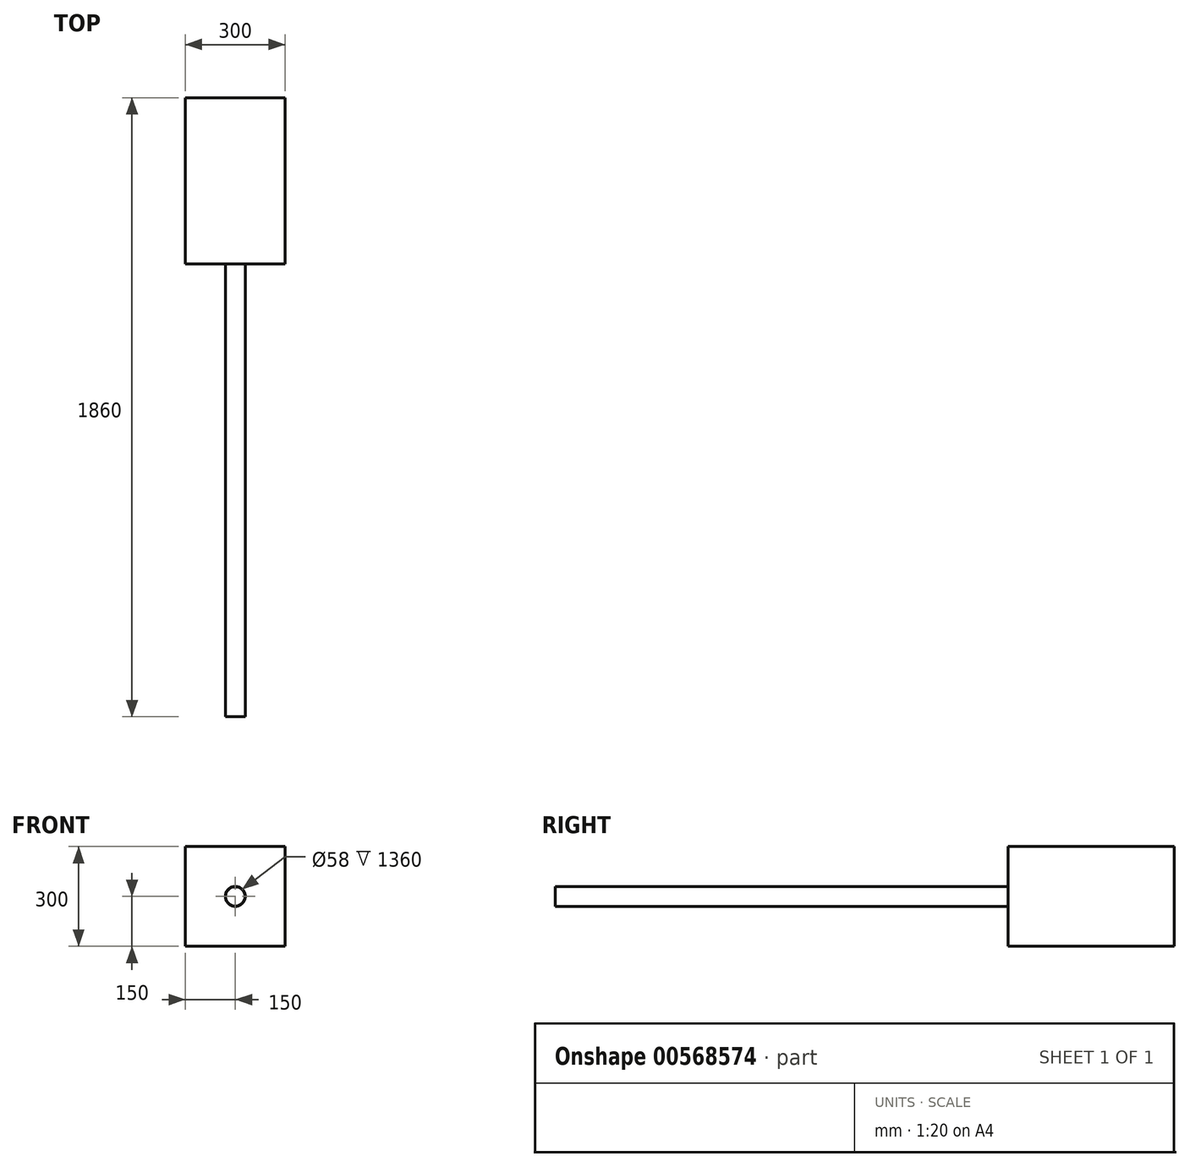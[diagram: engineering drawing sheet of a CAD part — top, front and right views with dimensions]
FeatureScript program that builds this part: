
annotation { "Feature Type Name" : "Feature", "Feature Type Description" : "" }
export const myFeature = defineFeature(function(context is Context, id is Id, definition is map)
    precondition{}
    {
        {
            var Q0;
            Q0=qCreatedBy(makeId("Front.planeOp"),FACE);
            var sketch = newSketch(context, id + "F0", { "sketchPlane" : qUnion([Q0])});
            skCircle(sketch, "E0", {"center": v(0, 0) * mm, "radius": 30 * mm});
            skSolve(sketch);
        }
        {
            var Q0;
            Q0 = qSketchRegion(id + "F0", true);
            extrude(context, id + "F1", {"entities" : qUnion([Q0]), "depth" : 1500 * mm, "offsetDistance" : 25 * mm});
        }
        {
            var Q0;
            Q0=makeQuery(id+"F1.opExtrude","CAP_FACE",FACE,{"disambiguationData":[OSD([sQuery(id+"F0.wireOp",EDGE,"E0")])],"isStart":false});
            var sketch = newSketch(context, id + "F2", { "sketchPlane" : qUnion([Q0])});
            skCircle(sketch, "E1", {"center": v(0, 0) * mm, "radius": 29 * mm});
            skSolve(sketch);
        }
        {
            var Q0;
            Q0=makeQuery(id+"F2.imprint","IMPRINT",FACE,{"disambiguationData":[TD([[makeQuery(id+"F2.imprint","IMPRINT",EDGE,{"derivedFrom":sQuery(id+"F2.wireOp",EDGE,"E1")}),1.0]])]});
            extrude(context, id + "F3", {"entities" : qUnion([Q0]), "operationType" : NewBodyOperationType.REMOVE, "oppositeDirection" : true, "depth" : 1500 * mm, "offsetDistance" : 25 * mm});
        }
        {
            var Q0;
            Q0=qCreatedBy(makeId("Front.planeOp"),FACE);
            var sketch = newSketch(context, id + "F4", { "sketchPlane" : qUnion([Q0])});
            skCircle(sketch, "E2", {"center": v(0, 0) * mm, "radius": 6 * mm});
            skSolve(sketch);
        }
        {
            var Q0;
            Q0=sQuery(id+"F4.wireOp",EDGE,"E2");
            extrude(context, id + "F5", {"bodyType" : ToolBodyType.SURFACE, "surfaceEntities" : qUnion([Q0]), "oppositeDirection" : true, "depth" : 400 * mm, "offsetDistance" : 25 * mm, "hasSecondDirection" : true, "secondDirectionOppositeDirection" : false, "secondDirectionDepth" : 100 * mm});
        }
        {
            var Q0;
            Q0=qCreatedBy(makeId("Right.planeOp"),FACE);
            var sketch = newSketch(context, id + "F6", { "sketchPlane" : qUnion([Q0])});
            skLineSegment(sketch, "E3", {"start": v(-140, 0) * mm, "end": v(-140, 150) * mm});
            skLineSegment(sketch, "E4", {"start": v(-140, 150) * mm, "end": v(360, 150) * mm});
            skLineSegment(sketch, "E5", {"start": v(360, 150) * mm, "end": v(360, -150) * mm});
            skLineSegment(sketch, "E6", {"start": v(360, -150) * mm, "end": v(-140, -150) * mm});
            skLineSegment(sketch, "E7", {"start": v(-140, -150) * mm, "end": v(-140, 0) * mm});
            skSolve(sketch);
        }
        {
            var Q0;
            Q0 = qSketchRegion(id + "F6", true);
            extrude(context, id + "F7", {"entities" : qUnion([Q0]), "operationType" : NewBodyOperationType.ADD, "depth" : 150 * mm, "offsetDistance" : 25 * mm, "hasSecondDirection" : true, "secondDirectionOppositeDirection" : true, "secondDirectionDepth" : 150 * mm});
        }
    });
